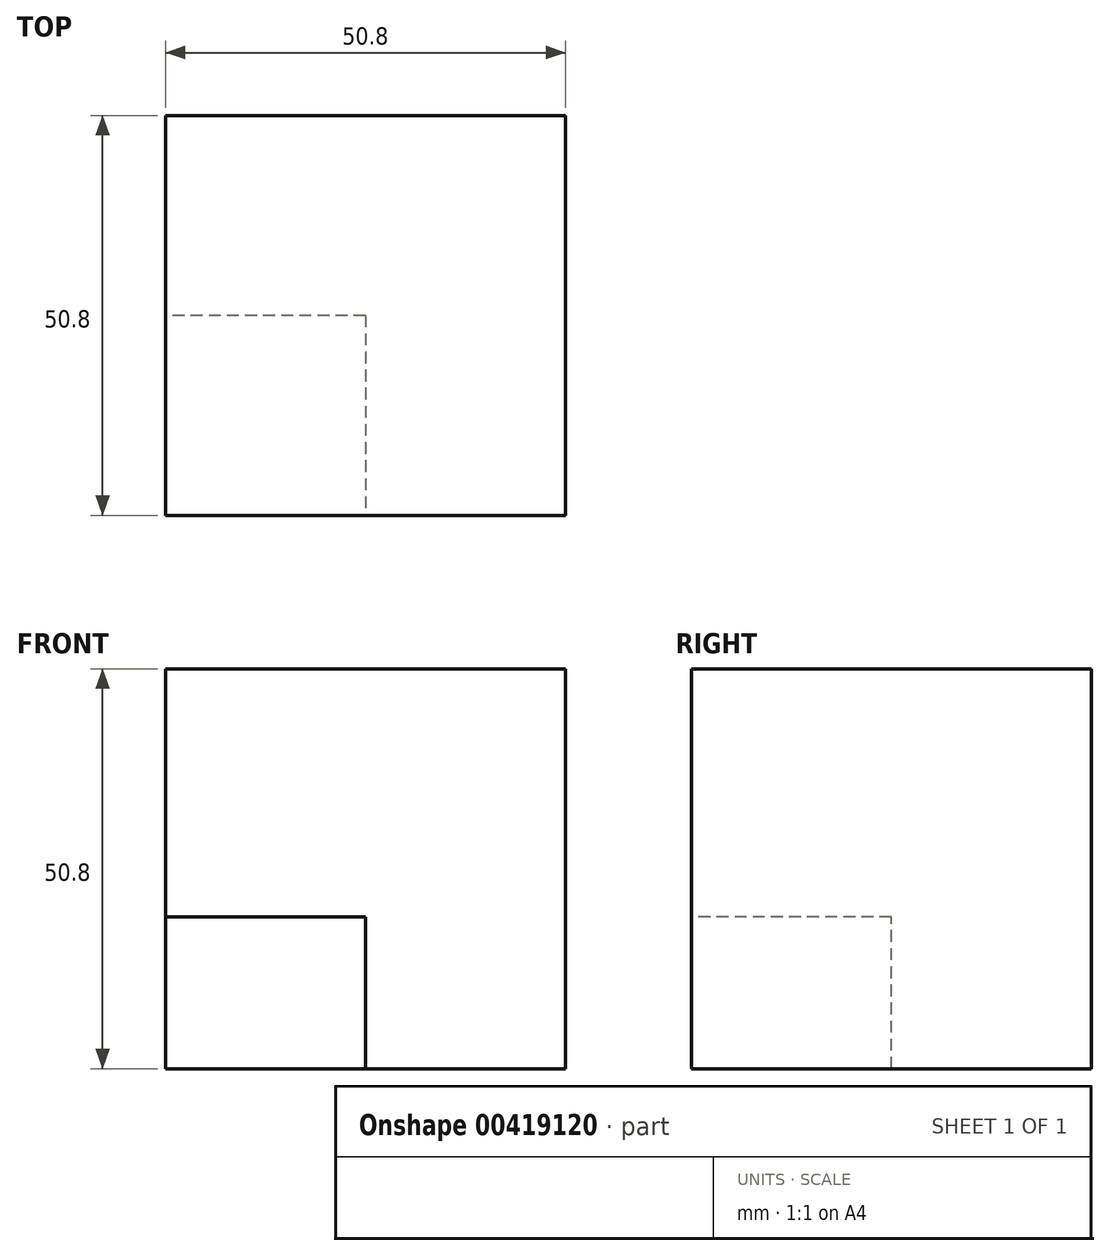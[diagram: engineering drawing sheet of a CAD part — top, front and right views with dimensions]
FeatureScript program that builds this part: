
annotation { "Feature Type Name" : "Feature", "Feature Type Description" : "" }
export const myFeature = defineFeature(function(context is Context, id is Id, definition is map)
    precondition{}
    {
        {
            var Q0;
            Q0=qCreatedBy(makeId("Front.planeOp"),FACE);
            var sketch = newSketch(context, id + "F0", { "sketchPlane" : qUnion([Q0])});
            skLineSegment(sketch, "E0", {"start": v(0, 0) * mm, "end": v(-50.8, 0) * mm});
            skLineSegment(sketch, "E1", {"start": v(-50.8, 0) * mm, "end": v(-50.8, 50.8) * mm});
            skLineSegment(sketch, "E2", {"start": v(-50.8, 50.8) * mm, "end": v(0, 50.8) * mm});
            skLineSegment(sketch, "E3", {"start": v(0, 0) * mm, "end": v(0, 50.8) * mm});
            skSolve(sketch);
        }
        {
            var Q0;
            Q0 = qSketchRegion(id + "F0", true);
            extrude(context, id + "F1", {"entities" : qUnion([Q0]), "depth" : 50.8 * mm});
        }
        {
            var Q0;
            Q0=qCreatedBy(makeId("Front.planeOp"),FACE);
            var sketch = newSketch(context, id + "F2", { "sketchPlane" : qUnion([Q0])});
            skLineSegment(sketch, "E4.bottom", {"start": v(-50.22, 0) * mm, "end": v(-24.82, 0) * mm});
            skLineSegment(sketch, "E4.top", {"start": v(-50.22, 25.4) * mm, "end": v(-24.82, 25.4) * mm});
            skLineSegment(sketch, "E4.left", {"start": v(-50.22, 0) * mm, "end": v(-50.22, 25.4) * mm});
            skLineSegment(sketch, "E4.right", {"start": v(-24.82, 0) * mm, "end": v(-24.82, 25.4) * mm});
            skSolve(sketch);
        }
        {
            var Q0;
            Q0 = qSketchRegion(id + "F2", true);
            extrude(context, id + "F3", {"entities" : qUnion([Q0]), "operationType" : NewBodyOperationType.REMOVE, "oppositeDirection" : true, "depth" : 25.4 * mm});
        }
        {
            var Q0;
            Q0=qCreatedBy(makeId("Front.planeOp"),FACE);
            var sketch = newSketch(context, id + "F4", { "sketchPlane" : qUnion([Q0])});
            skLineSegment(sketch, "E5.bottom", {"start": v(-50.03, 0) * mm, "end": v(-24.63, 0) * mm});
            skLineSegment(sketch, "E5.top", {"start": v(-50.03, 25.4) * mm, "end": v(-24.63, 25.4) * mm});
            skLineSegment(sketch, "E5.left", {"start": v(-50.03, 0) * mm, "end": v(-50.03, 25.4) * mm});
            skLineSegment(sketch, "E5.right", {"start": v(-24.63, 0) * mm, "end": v(-24.63, 25.4) * mm});
            skSolve(sketch);
        }
        {
            var Q0;
            Q0 = qSketchRegion(id + "F4", true);
            extrude(context, id + "F5", {"entities" : qUnion([Q0]), "operationType" : NewBodyOperationType.REMOVE, "oppositeDirection" : true, "depth" : 25.4 * mm});
        }
        {
            var Q0;
            Q0=makeQuery(id+"F1.opExtrude","CAP_FACE",FACE,{"disambiguationData":[OSD([sQuery(id+"F0.wireOp",EDGE,"E0"),sQuery(id+"F0.wireOp",EDGE,"E1"),sQuery(id+"F0.wireOp",EDGE,"E2"),sQuery(id+"F0.wireOp",EDGE,"E3")])],"isStart":false});
            var sketch = newSketch(context, id + "F6", { "sketchPlane" : qUnion([Q0])});
            skLineSegment(sketch, "E6.bottom", {"start": v(-50.8, 0) * mm, "end": v(-25.4, 0) * mm});
            skLineSegment(sketch, "E6.top", {"start": v(-50.8, 19.29) * mm, "end": v(-25.4, 19.29) * mm});
            skLineSegment(sketch, "E6.left", {"start": v(-50.8, 0) * mm, "end": v(-50.8, 19.29) * mm});
            skLineSegment(sketch, "E6.right", {"start": v(-25.4, 0) * mm, "end": v(-25.4, 19.29) * mm});
            skSolve(sketch);
        }
        {
            var Q0;
            Q0=makeQuery(id+"F6.imprint","IMPRINT",FACE,{"disambiguationData":[TD([[makeQuery(id+"F6.imprint","IMPRINT",EDGE,{"derivedFrom":sQuery(id+"F6.wireOp",EDGE,"E6.bottom")}),-1.0]])]});
            extrude(context, id + "F7", {"entities" : qUnion([Q0]), "operationType" : NewBodyOperationType.REMOVE, "oppositeDirection" : true, "depth" : 25.4 * mm});
        }
    });
